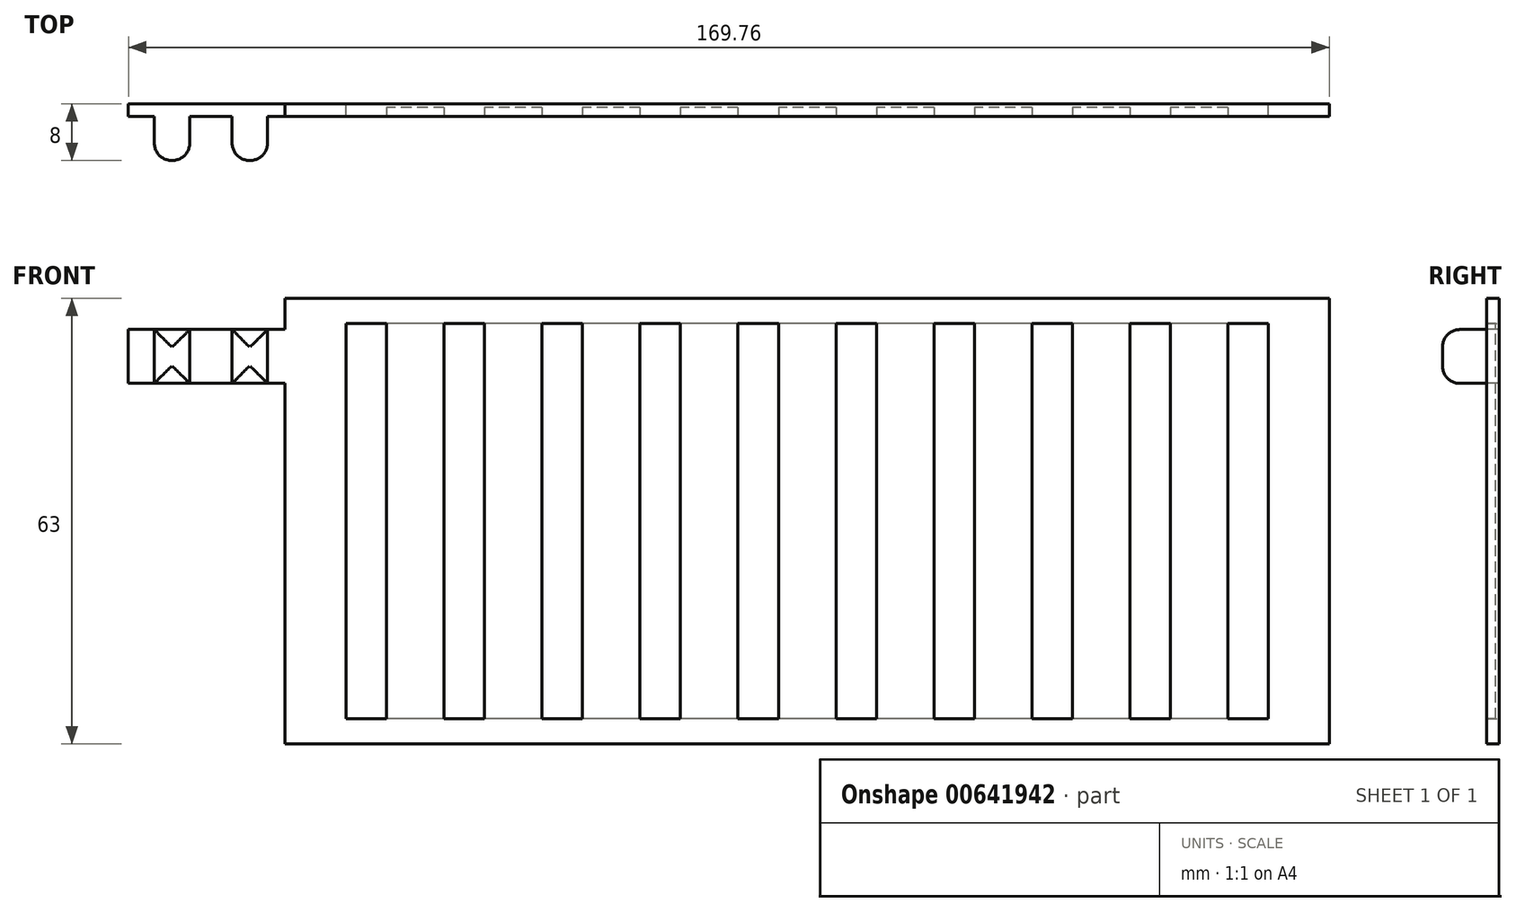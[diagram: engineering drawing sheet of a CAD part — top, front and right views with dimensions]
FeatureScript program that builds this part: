
annotation { "Feature Type Name" : "Feature", "Feature Type Description" : "" }
export const myFeature = defineFeature(function(context is Context, id is Id, definition is map)
    precondition{}
    {
        {
            var Q0;
            Q0=qCreatedBy(makeId("Front.planeOp"),FACE);
            var sketch = newSketch(context, id + "F0", { "sketchPlane" : qUnion([Q0])});
            skLineSegment(sketch, "E0.bottom", {"start": v(73.81, -31.5) * mm, "end": v(-73.81, -31.5) * mm});
            skLineSegment(sketch, "E0.top", {"start": v(73.81, 31.5) * mm, "end": v(-73.81, 31.5) * mm});
            skLineSegment(sketch, "E0.left", {"start": v(73.81, -31.5) * mm, "end": v(73.81, 31.5) * mm});
            skLineSegment(sketch, "E0.right", {"start": v(-73.81, -31.5) * mm, "end": v(-73.81, 31.5) * mm});
            skPoint(sketch, "E0.middle", {"position": v(0, 0) * mm});
            skLineSegment(sketch, "E1.bottom", {"start": v(65.18, -27.94) * mm, "end": v(-65.18, -27.94) * mm});
            skLineSegment(sketch, "E1.top", {"start": v(65.18, 27.94) * mm, "end": v(-65.18, 27.94) * mm});
            skLineSegment(sketch, "E1.left", {"start": v(65.18, -27.94) * mm, "end": v(65.18, 27.94) * mm});
            skLineSegment(sketch, "E1.right", {"start": v(-65.18, -27.94) * mm, "end": v(-65.18, 27.94) * mm});
            skSolve(sketch);
        }
        {
            var Q0;
            Q0=makeQuery(id+"F0.imprint","IMPRINT",FACE,{"disambiguationData":[TD([[makeQuery(id+"F0.imprint","IMPRINT",EDGE,{"derivedFrom":sQuery(id+"F0.wireOp",EDGE,"E0.bottom")}),-1.0]])]});
            extrude(context, id + "F1", {"entities" : qUnion([Q0]), "depth" : 1.78 * mm});
        }
        {
            var Q0;
            Q0=makeQuery(id+"F1.opExtrude","CAP_FACE",FACE,{"disambiguationData":[OSD([sQuery(id+"F0.wireOp",EDGE,"E0.bottom"),sQuery(id+"F0.wireOp",EDGE,"E0.top"),sQuery(id+"F0.wireOp",EDGE,"E0.left"),sQuery(id+"F0.wireOp",EDGE,"E0.right"),sQuery(id+"F0.wireOp",EDGE,"E1.bottom"),sQuery(id+"F0.wireOp",EDGE,"E1.top"),sQuery(id+"F0.wireOp",EDGE,"E1.left"),sQuery(id+"F0.wireOp",EDGE,"E1.right")])],"isStart":false});
            var sketch = newSketch(context, id + "F2", { "sketchPlane" : qUnion([Q0])});
            skLineSegment(sketch, "E2.bottom", {"start": v(-51.33, -27.94) * mm, "end": v(-59.46, -27.94) * mm});
            skLineSegment(sketch, "E2.top", {"start": v(-51.33, 27.94) * mm, "end": v(-59.46, 27.94) * mm});
            skLineSegment(sketch, "E2.left", {"start": v(-51.33, -27.94) * mm, "end": v(-51.33, 27.94) * mm});
            skLineSegment(sketch, "E2.right", {"start": v(-59.46, -27.94) * mm, "end": v(-59.46, 27.94) * mm});
            skPoint(sketch, "E2.middle", {"position": v(-55.4, 0) * mm});
            skLineSegment(sketch, "E3", {"start": v(-65.18, 27.94) * mm, "end": v(-65.18, 47.6) * mm, "construction": true});
            skLineSegment(sketch, "E4", {"start": v(65.18, 27.94) * mm, "end": v(65.18, 47.82) * mm, "construction": true});
            skPoint(sketch, "E5.1.0.0", {"position": v(-41.54, 0) * mm});
            skLineSegment(sketch, "E5.1.0.1", {"start": v(-37.48, -27.94) * mm, "end": v(-45.6, -27.94) * mm});
            skLineSegment(sketch, "E5.1.0.2", {"start": v(-37.48, 27.94) * mm, "end": v(-45.6, 27.94) * mm});
            skLineSegment(sketch, "E5.1.0.3", {"start": v(-37.48, -27.94) * mm, "end": v(-37.48, 27.94) * mm});
            skLineSegment(sketch, "E5.1.0.4", {"start": v(-45.6, -27.94) * mm, "end": v(-45.6, 27.94) * mm});
            skPoint(sketch, "E5.2.0.0", {"position": v(-27.7, 0) * mm});
            skLineSegment(sketch, "E5.2.0.1", {"start": v(-23.63, -27.94) * mm, "end": v(-31.76, -27.94) * mm});
            skLineSegment(sketch, "E5.2.0.2", {"start": v(-23.63, 27.94) * mm, "end": v(-31.76, 27.94) * mm});
            skLineSegment(sketch, "E5.2.0.3", {"start": v(-23.63, -27.94) * mm, "end": v(-23.63, 27.94) * mm});
            skLineSegment(sketch, "E5.2.0.4", {"start": v(-31.76, -27.94) * mm, "end": v(-31.76, 27.94) * mm});
            skPoint(sketch, "E5.3.0.0", {"position": v(-13.85, 0) * mm});
            skLineSegment(sketch, "E5.3.0.1", {"start": v(-9.78, -27.94) * mm, "end": v(-17.91, -27.94) * mm});
            skLineSegment(sketch, "E5.3.0.2", {"start": v(-9.78, 27.94) * mm, "end": v(-17.91, 27.94) * mm});
            skLineSegment(sketch, "E5.3.0.3", {"start": v(-9.78, -27.94) * mm, "end": v(-9.78, 27.94) * mm});
            skLineSegment(sketch, "E5.3.0.4", {"start": v(-17.91, -27.94) * mm, "end": v(-17.91, 27.94) * mm});
            skPoint(sketch, "E5.4.0.0", {"position": v(0, 0) * mm});
            skLineSegment(sketch, "E5.4.0.1", {"start": v(4.06, -27.94) * mm, "end": v(-4.06, -27.94) * mm});
            skLineSegment(sketch, "E5.4.0.2", {"start": v(4.06, 27.94) * mm, "end": v(-4.06, 27.94) * mm});
            skLineSegment(sketch, "E5.4.0.3", {"start": v(4.06, -27.94) * mm, "end": v(4.06, 27.94) * mm});
            skLineSegment(sketch, "E5.4.0.4", {"start": v(-4.06, -27.94) * mm, "end": v(-4.06, 27.94) * mm});
            skPoint(sketch, "E5.5.0.0", {"position": v(13.85, 0) * mm});
            skLineSegment(sketch, "E5.5.0.1", {"start": v(17.91, -27.94) * mm, "end": v(9.78, -27.94) * mm});
            skLineSegment(sketch, "E5.5.0.2", {"start": v(17.91, 27.94) * mm, "end": v(9.78, 27.94) * mm});
            skLineSegment(sketch, "E5.5.0.3", {"start": v(17.91, -27.94) * mm, "end": v(17.91, 27.94) * mm});
            skLineSegment(sketch, "E5.5.0.4", {"start": v(9.78, -27.94) * mm, "end": v(9.78, 27.94) * mm});
            skPoint(sketch, "E5.6.0.0", {"position": v(27.7, 0) * mm});
            skLineSegment(sketch, "E5.6.0.1", {"start": v(31.76, -27.94) * mm, "end": v(23.63, -27.94) * mm});
            skLineSegment(sketch, "E5.6.0.2", {"start": v(31.76, 27.94) * mm, "end": v(23.63, 27.94) * mm});
            skLineSegment(sketch, "E5.6.0.3", {"start": v(31.76, -27.94) * mm, "end": v(31.76, 27.94) * mm});
            skLineSegment(sketch, "E5.6.0.4", {"start": v(23.63, -27.94) * mm, "end": v(23.63, 27.94) * mm});
            skPoint(sketch, "E5.7.0.0", {"position": v(41.54, 0) * mm});
            skLineSegment(sketch, "E5.7.0.1", {"start": v(45.6, -27.94) * mm, "end": v(37.48, -27.94) * mm});
            skLineSegment(sketch, "E5.7.0.2", {"start": v(45.6, 27.94) * mm, "end": v(37.48, 27.94) * mm});
            skLineSegment(sketch, "E5.7.0.3", {"start": v(45.6, -27.94) * mm, "end": v(45.6, 27.94) * mm});
            skLineSegment(sketch, "E5.7.0.4", {"start": v(37.48, -27.94) * mm, "end": v(37.48, 27.94) * mm});
            skPoint(sketch, "E5.8.0.0", {"position": v(55.4, 0) * mm});
            skLineSegment(sketch, "E5.8.0.1", {"start": v(59.46, -27.94) * mm, "end": v(51.33, -27.94) * mm});
            skLineSegment(sketch, "E5.8.0.2", {"start": v(59.46, 27.94) * mm, "end": v(51.33, 27.94) * mm});
            skLineSegment(sketch, "E5.8.0.3", {"start": v(59.46, -27.94) * mm, "end": v(59.46, 27.94) * mm});
            skLineSegment(sketch, "E5.8.0.4", {"start": v(51.33, -27.94) * mm, "end": v(51.33, 27.94) * mm});
            skLineSegment(sketch, "E5.direction1", {"start": v(-59.46, -27.94) * mm, "end": v(-45.6, -27.94) * mm, "construction": true});
            skSolve(sketch);
        }
        {
            var Q0;
            Q0=qSketchRegion(id+"F2",true);
            extrude(context, id + "F3", {"entities" : qUnion([Q0]), "operationType" : NewBodyOperationType.ADD, "oppositeDirection" : true, "depth" : 1.27 * mm});
        }
        {
            var Q0;
            Q0=makeQuery(id+"F3.boolean.opBoolean","MERGE",FACE,{"derivedFrom":[makeQuery(id+"F1.opExtrude","CAP_FACE",FACE,{"disambiguationData":[OSD([sQuery(id+"F0.wireOp",EDGE,"E0.bottom"),sQuery(id+"F0.wireOp",EDGE,"E0.top"),sQuery(id+"F0.wireOp",EDGE,"E0.left"),sQuery(id+"F0.wireOp",EDGE,"E0.right"),sQuery(id+"F0.wireOp",EDGE,"E1.bottom"),sQuery(id+"F0.wireOp",EDGE,"E1.top"),sQuery(id+"F0.wireOp",EDGE,"E1.left"),sQuery(id+"F0.wireOp",EDGE,"E1.right")])],"isStart":false}),makeQuery(id+"F3.opExtrude","CAP_FACE",FACE,{"disambiguationData":[OSD([sQuery(id+"F2.wireOp",EDGE,"E2.bottom"),sQuery(id+"F2.wireOp",EDGE,"E2.top"),sQuery(id+"F2.wireOp",EDGE,"E2.left"),sQuery(id+"F2.wireOp",EDGE,"E2.right")])],"isStart":true}),makeQuery(id+"F3.opExtrude","CAP_FACE",FACE,{"disambiguationData":[OSD([sQuery(id+"F2.wireOp",EDGE,"E5.1.0.1"),sQuery(id+"F2.wireOp",EDGE,"E5.1.0.2"),sQuery(id+"F2.wireOp",EDGE,"E5.1.0.3"),sQuery(id+"F2.wireOp",EDGE,"E5.1.0.4")])],"isStart":true}),makeQuery(id+"F3.opExtrude","CAP_FACE",FACE,{"disambiguationData":[OSD([sQuery(id+"F2.wireOp",EDGE,"E5.2.0.1"),sQuery(id+"F2.wireOp",EDGE,"E5.2.0.2"),sQuery(id+"F2.wireOp",EDGE,"E5.2.0.3"),sQuery(id+"F2.wireOp",EDGE,"E5.2.0.4")])],"isStart":true}),makeQuery(id+"F3.opExtrude","CAP_FACE",FACE,{"disambiguationData":[OSD([sQuery(id+"F2.wireOp",EDGE,"E5.3.0.1"),sQuery(id+"F2.wireOp",EDGE,"E5.3.0.2"),sQuery(id+"F2.wireOp",EDGE,"E5.3.0.3"),sQuery(id+"F2.wireOp",EDGE,"E5.3.0.4")])],"isStart":true}),makeQuery(id+"F3.opExtrude","CAP_FACE",FACE,{"disambiguationData":[OSD([sQuery(id+"F2.wireOp",EDGE,"E5.4.0.1"),sQuery(id+"F2.wireOp",EDGE,"E5.4.0.2"),sQuery(id+"F2.wireOp",EDGE,"E5.4.0.3"),sQuery(id+"F2.wireOp",EDGE,"E5.4.0.4")])],"isStart":true}),makeQuery(id+"F3.opExtrude","CAP_FACE",FACE,{"disambiguationData":[OSD([sQuery(id+"F2.wireOp",EDGE,"E5.5.0.1"),sQuery(id+"F2.wireOp",EDGE,"E5.5.0.2"),sQuery(id+"F2.wireOp",EDGE,"E5.5.0.3"),sQuery(id+"F2.wireOp",EDGE,"E5.5.0.4")])],"isStart":true}),makeQuery(id+"F3.opExtrude","CAP_FACE",FACE,{"disambiguationData":[OSD([sQuery(id+"F2.wireOp",EDGE,"E5.6.0.1"),sQuery(id+"F2.wireOp",EDGE,"E5.6.0.2"),sQuery(id+"F2.wireOp",EDGE,"E5.6.0.3"),sQuery(id+"F2.wireOp",EDGE,"E5.6.0.4")])],"isStart":true}),makeQuery(id+"F3.opExtrude","CAP_FACE",FACE,{"disambiguationData":[OSD([sQuery(id+"F2.wireOp",EDGE,"E5.7.0.1"),sQuery(id+"F2.wireOp",EDGE,"E5.7.0.2"),sQuery(id+"F2.wireOp",EDGE,"E5.7.0.3"),sQuery(id+"F2.wireOp",EDGE,"E5.7.0.4")])],"isStart":true}),makeQuery(id+"F3.opExtrude","CAP_FACE",FACE,{"disambiguationData":[OSD([sQuery(id+"F2.wireOp",EDGE,"E5.8.0.1"),sQuery(id+"F2.wireOp",EDGE,"E5.8.0.2"),sQuery(id+"F2.wireOp",EDGE,"E5.8.0.3"),sQuery(id+"F2.wireOp",EDGE,"E5.8.0.4")])],"isStart":true})]});
            var sketch = newSketch(context, id + "F4", { "sketchPlane" : qUnion([Q0])});
            skLineSegment(sketch, "E6.left", {"start": v(-65.18, 27.09) * mm, "end": v(-65.18, 19.47) * mm});
            skLineSegment(sketch, "E6.right", {"start": v(-95.95, 27.09) * mm, "end": v(-95.95, 19.47) * mm});
            skLineSegment(sketch, "E7", {"start": v(-95.95, 27.09) * mm, "end": v(-65.18, 27.09) * mm});
            skLineSegment(sketch, "E8", {"start": v(-95.95, 19.47) * mm, "end": v(-65.18, 19.47) * mm});
            skSolve(sketch);
        }
        {
            var Q0;
            Q0=qSketchRegion(id+"F4",true);
            extrude(context, id + "F5", {"entities" : qUnion([Q0]), "operationType" : NewBodyOperationType.ADD, "oppositeDirection" : true, "depth" : 1.78 * mm});
        }
        {
            var Q0;
            Q0=makeQuery(id+"F5.boolean.opBoolean","MERGE",FACE,{"derivedFrom":[makeQuery(id+"F3.boolean.opBoolean","MERGE",FACE,{"derivedFrom":[makeQuery(id+"F1.opExtrude","CAP_FACE",FACE,{"disambiguationData":[OSD([sQuery(id+"F0.wireOp",EDGE,"E0.bottom"),sQuery(id+"F0.wireOp",EDGE,"E0.top"),sQuery(id+"F0.wireOp",EDGE,"E0.left"),sQuery(id+"F0.wireOp",EDGE,"E0.right"),sQuery(id+"F0.wireOp",EDGE,"E1.bottom"),sQuery(id+"F0.wireOp",EDGE,"E1.top"),sQuery(id+"F0.wireOp",EDGE,"E1.left"),sQuery(id+"F0.wireOp",EDGE,"E1.right")])],"isStart":false}),makeQuery(id+"F3.opExtrude","CAP_FACE",FACE,{"disambiguationData":[OSD([sQuery(id+"F2.wireOp",EDGE,"E2.bottom"),sQuery(id+"F2.wireOp",EDGE,"E2.top"),sQuery(id+"F2.wireOp",EDGE,"E2.left"),sQuery(id+"F2.wireOp",EDGE,"E2.right")])],"isStart":true}),makeQuery(id+"F3.opExtrude","CAP_FACE",FACE,{"disambiguationData":[OSD([sQuery(id+"F2.wireOp",EDGE,"E5.1.0.1"),sQuery(id+"F2.wireOp",EDGE,"E5.1.0.2"),sQuery(id+"F2.wireOp",EDGE,"E5.1.0.3"),sQuery(id+"F2.wireOp",EDGE,"E5.1.0.4")])],"isStart":true}),makeQuery(id+"F3.opExtrude","CAP_FACE",FACE,{"disambiguationData":[OSD([sQuery(id+"F2.wireOp",EDGE,"E5.2.0.1"),sQuery(id+"F2.wireOp",EDGE,"E5.2.0.2"),sQuery(id+"F2.wireOp",EDGE,"E5.2.0.3"),sQuery(id+"F2.wireOp",EDGE,"E5.2.0.4")])],"isStart":true}),makeQuery(id+"F3.opExtrude","CAP_FACE",FACE,{"disambiguationData":[OSD([sQuery(id+"F2.wireOp",EDGE,"E5.3.0.1"),sQuery(id+"F2.wireOp",EDGE,"E5.3.0.2"),sQuery(id+"F2.wireOp",EDGE,"E5.3.0.3"),sQuery(id+"F2.wireOp",EDGE,"E5.3.0.4")])],"isStart":true}),makeQuery(id+"F3.opExtrude","CAP_FACE",FACE,{"disambiguationData":[OSD([sQuery(id+"F2.wireOp",EDGE,"E5.4.0.1"),sQuery(id+"F2.wireOp",EDGE,"E5.4.0.2"),sQuery(id+"F2.wireOp",EDGE,"E5.4.0.3"),sQuery(id+"F2.wireOp",EDGE,"E5.4.0.4")])],"isStart":true}),makeQuery(id+"F3.opExtrude","CAP_FACE",FACE,{"disambiguationData":[OSD([sQuery(id+"F2.wireOp",EDGE,"E5.5.0.1"),sQuery(id+"F2.wireOp",EDGE,"E5.5.0.2"),sQuery(id+"F2.wireOp",EDGE,"E5.5.0.3"),sQuery(id+"F2.wireOp",EDGE,"E5.5.0.4")])],"isStart":true}),makeQuery(id+"F3.opExtrude","CAP_FACE",FACE,{"disambiguationData":[OSD([sQuery(id+"F2.wireOp",EDGE,"E5.6.0.1"),sQuery(id+"F2.wireOp",EDGE,"E5.6.0.2"),sQuery(id+"F2.wireOp",EDGE,"E5.6.0.3"),sQuery(id+"F2.wireOp",EDGE,"E5.6.0.4")])],"isStart":true}),makeQuery(id+"F3.opExtrude","CAP_FACE",FACE,{"disambiguationData":[OSD([sQuery(id+"F2.wireOp",EDGE,"E5.7.0.1"),sQuery(id+"F2.wireOp",EDGE,"E5.7.0.2"),sQuery(id+"F2.wireOp",EDGE,"E5.7.0.3"),sQuery(id+"F2.wireOp",EDGE,"E5.7.0.4")])],"isStart":true}),makeQuery(id+"F3.opExtrude","CAP_FACE",FACE,{"disambiguationData":[OSD([sQuery(id+"F2.wireOp",EDGE,"E5.8.0.1"),sQuery(id+"F2.wireOp",EDGE,"E5.8.0.2"),sQuery(id+"F2.wireOp",EDGE,"E5.8.0.3"),sQuery(id+"F2.wireOp",EDGE,"E5.8.0.4")])],"isStart":true})]}),makeQuery(id+"F5.opExtrude","CAP_FACE",FACE,{"disambiguationData":[OSD([sQuery(id+"F4.wireOp",EDGE,"E6.bottom"),sQuery(id+"F4.wireOp",EDGE,"E6.top"),sQuery(id+"F4.wireOp",EDGE,"E6.left"),sQuery(id+"F4.wireOp",EDGE,"E6.right")])],"isStart":true})]});
            var sketch = newSketch(context, id + "F6", { "sketchPlane" : qUnion([Q0])});
            skSolve(sketch);
        }
        {
            var Q0;
            {var subQ24=sQuery(id+"F0.wireOp",EDGE,"E0.bottom");Q0=makeQuery(id+"F6.imprint","IMPRINT",FACE,{"disambiguationData":[TD([[makeQuery(id+"F6.imprint","IMPRINT",EDGE,{"derivedFrom":makeQuery(id+"F1.opExtrude","CAP_EDGE",EDGE,{"disambiguationData":[OSD([subQ24])],"isStart":false})}),-1.0]])]});}
            var sketch = newSketch(context, id + "F7", { "sketchPlane" : qUnion([Q0])});
            skLineSegment(sketch, "E9.bottom", {"start": v(-87.29, 27.09) * mm, "end": v(-92.29, 27.09) * mm});
            skLineSegment(sketch, "E9.top", {"start": v(-87.29, 19.47) * mm, "end": v(-92.29, 19.47) * mm});
            skLineSegment(sketch, "E9.left", {"start": v(-87.29, 27.09) * mm, "end": v(-87.29, 19.47) * mm});
            skLineSegment(sketch, "E9.right", {"start": v(-92.29, 27.09) * mm, "end": v(-92.29, 19.47) * mm});
            skPoint(sketch, "E9.middle", {"position": v(-89.79, 23.28) * mm});
            skLineSegment(sketch, "E10.bottom", {"start": v(-81.3, 27.09) * mm, "end": v(-76.29, 27.09) * mm});
            skLineSegment(sketch, "E10.top", {"start": v(-81.3, 19.47) * mm, "end": v(-76.29, 19.47) * mm});
            skLineSegment(sketch, "E10.left", {"start": v(-81.3, 27.09) * mm, "end": v(-81.3, 19.47) * mm});
            skLineSegment(sketch, "E10.right", {"start": v(-76.29, 27.09) * mm, "end": v(-76.29, 19.47) * mm});
            skSolve(sketch);
        }
        {
            var Q0;
            Q0=qSketchRegion(id+"F7",true);
            extrude(context, id + "F8", {"entities" : qUnion([Q0]), "operationType" : NewBodyOperationType.ADD, "depth" : 6.22 * mm});
        }
        {
            var Q0;
            Q0=makeQuery(id+"F8.opExtrude","CAP_FACE",FACE,{"disambiguationData":[OSD([sQuery(id+"F7.wireOp",EDGE,"E9.bottom"),sQuery(id+"F7.wireOp",EDGE,"E9.top"),sQuery(id+"F7.wireOp",EDGE,"E9.left"),sQuery(id+"F7.wireOp",EDGE,"E9.right")])],"isStart":false});
            fillet(context, id + "F9", {"entities" : qUnion([Q0]), "radius" : 2.44 * mm, "tangentPropagation" : true, "allowEdgeOverflow" : false});
        }
        {
            var Q0;
            Q0=makeQuery(id+"F8.opExtrude","CAP_FACE",FACE,{"disambiguationData":[OSD([sQuery(id+"F7.wireOp",EDGE,"E10.bottom"),sQuery(id+"F7.wireOp",EDGE,"E10.top"),sQuery(id+"F7.wireOp",EDGE,"E10.left"),sQuery(id+"F7.wireOp",EDGE,"E10.right")])],"isStart":false});
            fillet(context, id + "F10", {"entities" : qUnion([Q0]), "radius" : 2.44 * mm, "tangentPropagation" : true, "allowEdgeOverflow" : false});
        }
    });
